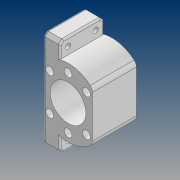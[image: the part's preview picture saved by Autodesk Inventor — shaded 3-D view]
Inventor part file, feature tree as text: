
AUTODESK INVENTOR PART (.ipt)
format: ipt  version: 2021 (Build 250183000, 183)  size: 206,336 bytes
history: native  units: mm
features: sketch x3, fillet x3, projected_geometry x3, extrude x2, reference x2, other x2, plane x1, hole x1, chamfer x1
ambient origin geometry x8: Origin, YZ Plane, XZ Plane, XY Plane, X Axis, Y Axis, Z Axis, Center Point
bodies: Solid1 (feature_tree)
feature tree (18):
  sketch  "Sketch1"  dims[d0=30.0mm d1=60.0mm]
  plane  "Work Plane1"
  extrude  "Extrusion1"  Depth=60.0mm
  hole  "Hole1"  [1 undecoded]
  extrude  "Extrusion2"  Depth=1.0mm
  chamfer  "Chamfer1"  Distance=5.0mm
  fillet  "Fillet1"  Radius=10.0mm
  fillet  "Fillet2"  [1 undecoded]
  fillet  "Fillet3"  Radius=2.0mm
  reference  "Reference1"
  sketch  "Sketch2"  dims[d2=30.0mm d3=21.0mm]
  projected_geometry  "Projected Loop1"
  projected_geometry  "Projected Loop2"
  sketch  "Sketch3"  dims[d4=30.5mm d5=0.0mm d7=5.0mm d9=5.0mm d10=3.2mm d11=6.0mm d12=4.0mm d13=2.0mm d14=90.0deg d15=8.0mm d16=20.594885mm d17=10.0mm d18=0.0mm d19=0.0mm d20=2.0mm d21=2.0mm d22=45.0deg d23=4.0mm d24=1.0mm d25=1.0mm]
  reference  "Reference2"
  projected_geometry  "Projected Loop3"
  other  "Assembly1"
  other  "1204 BALL NUT:1"
note: 2 required parameter values undecoded (feature->parameter linkage not recoverable at this tier; creation-order binding heuristic only, values carry confidence <= 0.55)
